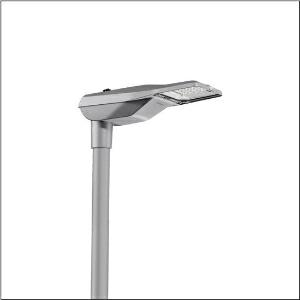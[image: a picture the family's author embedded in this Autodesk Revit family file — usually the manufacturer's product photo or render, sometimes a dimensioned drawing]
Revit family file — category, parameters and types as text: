
# Revit family: streetlight_sl_21_micro___pl52_5xe1h33s08db_2be5
name_source: partatom
category: Lighting Fixtures
units: mm (PartAtom-declared; Revit-internal decimal feet)

## family parameters
Cut with Voids When Loaded = No
Host = Face
Light Source = No
Part Type = Normal
Room Calculation Point = No
Round Connector Dimension = Use Diameter
Shared = No

## types (1)
- --- (1 x LED, 5020 lm, 39.1 W, 3000K)
    Apparent Load = 39 VA
    CIE Flux Codes = 27 59 98 100 100
    Color Rendering = 70
    Color Temperature = 3000K
    Default Elevation = 1800 mm
    Description = Streetlight SL 21 micro, mast luminaire, primary light control with lens, of PMMA, primary optical cover: cover, of toughened safety glass, transparent, light distribution: PL52, light emission: direct distribution, primary light characteristic: asymmetric, installation type: side-entry, post-top, LED, High Power LED, rated luminous flux: 5.020lm, luminous efficacy: 128lm/W, light colour: 730, colour temperature: 3000K, control: flexible luminous flux parameterisation, time-dependent luminous flux control, constant luminous flux control, overheat protection, pre-setting: logarithmic dimming characteristic, mains connection: 220..240V, AC, 50/60Hz, start of lifetime: 39W, end of service life: 41W, reduction: 18W, luminaire housing, of diecast aluminium, powder-coated, Siteco® metallic grey (DB 702S), corrosivity category C5 mid according to DIN EN ISO 12944, please order mast flange separately, inclination adjustable: 0°, 5°, 10°, 15°, sealing non-destructively replaceable, multi-level sealing system, length: 528mm, width: 235mm, height: 110mm, mast flange for spigot size: 42mm (side-entry): 5XC10008XM4, 60/48mm (side-entry/post-top): 5XC10108XM2, 76/60mm (side-entry/post-top): 5XC10108XM1, Smart Interface above, protection rating (complete): IP66, insulation class (complete): insulation class II (safety insulation), certification: CE, ENEC, ENEC+, VDE, impact resistance: IK09, permissible operating ambient temperature for outdoor applications: -40..+50°C, standard-compliant lighting for roads and squares, packaging unit: 1 piece

Light Distribution: PL52
    Height = 110 mm
    Lamp = 1 x LED
    Lamp Light Flux = 5020 lm
    Lamp Power = 39.1 W
    Lamp count = 1
    Length = 528 mm
    Luminous efficacy = 128 lm/W
    Manufacturer = Siteco
    ModVariant = No
    Model = 5XE1H33S08DB
    Number of Poles = 1
    OnlyDefault = Yes
    Power Factor = 1
    Product Name = Streetlight SL 21 micro | PL52
    Product group = mast luminaire | pylon top
    ProductGroupID = 6100
    Protection Class = Protection class II
    Protection Degree = IP 66
    RLX_Detail_Level = 1
    RLX_Emergency_Light_Flux = 0 lm
    RLX_Emergency_Type = 0
    RLX_Emergency_Type_DB = No
    RlxData = <blob elided: 108433 chars, md5=46b61912>
    Socket = socket
    Standby Power = 0 W
    System Light Flux = 5020 lm
    System Power = 39 W
    Type Comments = factory setting: luminous flux: 100 % | dim-lin: 254 | 765 mA
    Type Image = l_1277292.jpg
    URL = http://relux.com
    VarID = @adj_126621
    Voltage = 0 V
    Weight = 0.00 kg
    Width = 235 mm

## geometry (parser evidence)
native form markers: Blend x4, Sweep x9
no freeform markers — native parametric forms only
